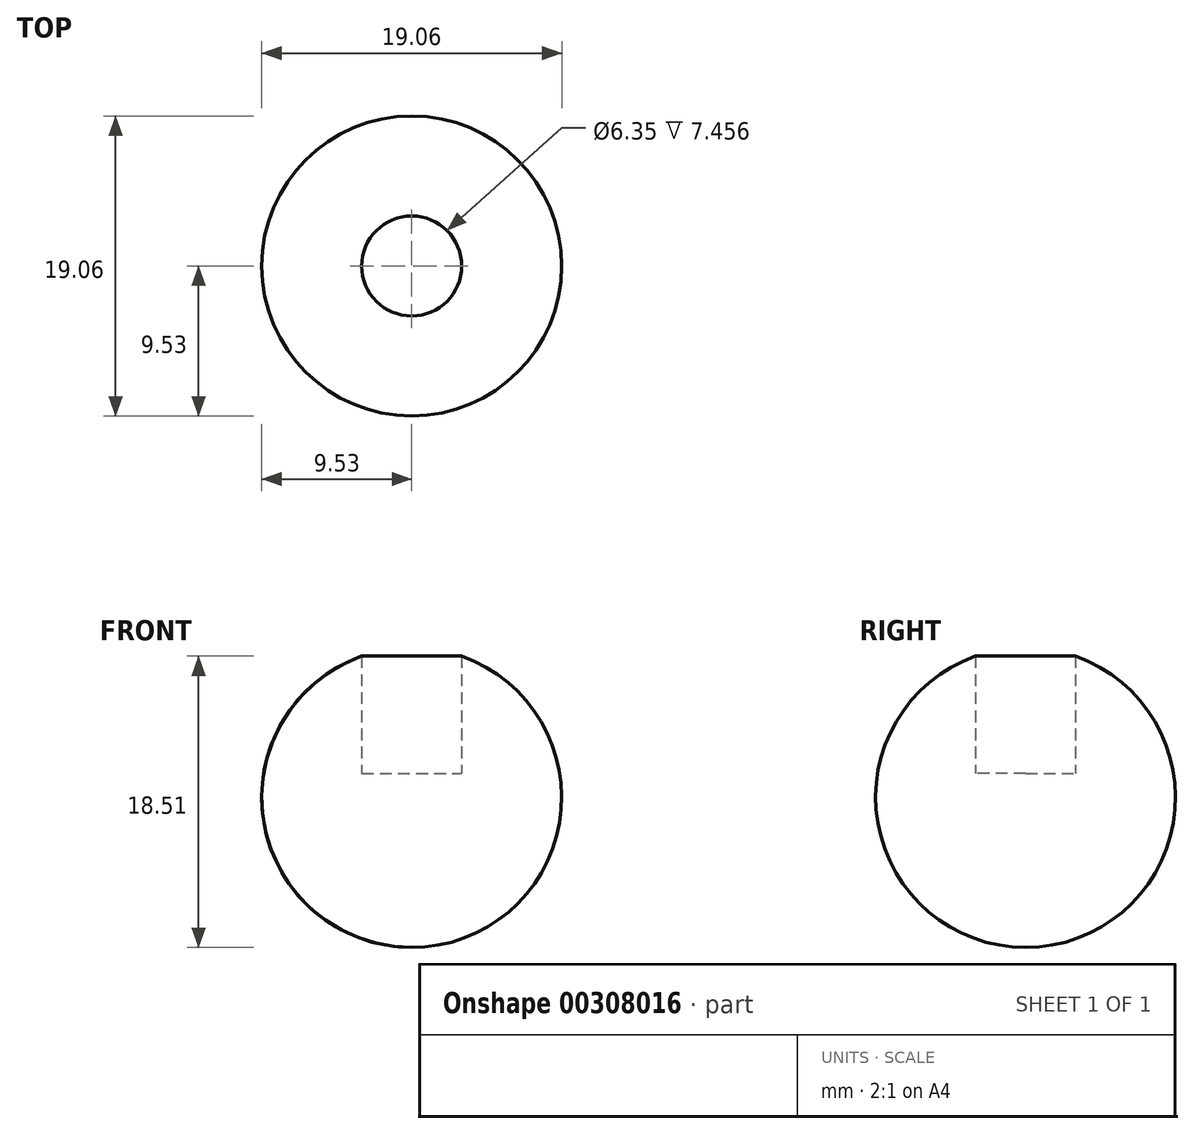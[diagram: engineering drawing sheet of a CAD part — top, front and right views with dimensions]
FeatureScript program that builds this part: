
annotation { "Feature Type Name" : "Feature", "Feature Type Description" : "" }
export const myFeature = defineFeature(function(context is Context, id is Id, definition is map)
    precondition{}
    {
        {
            var Q0;
            Q0=qCreatedBy(makeId("Front.planeOp"),FACE);
            var sketch = newSketch(context, id + "F0", { "sketchPlane" : qUnion([Q0])});
            skArc(sketch, "E0", {"start": v(0, 9.53) * mm, "mid": v(-9.53, 0) * mm, "end": v(0, -9.53) * mm});
            skLineSegment(sketch, "E1", {"start": v(0, 9.53) * mm, "end": v(0, -9.53) * mm});
            skSolve(sketch);
        }
        {
            var Q0;
            Q0=qCreatedBy(makeId("Top.planeOp"),FACE);
            var sketch = newSketch(context, id + "F1", { "sketchPlane" : qUnion([Q0])});
            skCircle(sketch, "E2", {"center": v(0, 0) * mm, "radius": 9.53 * mm});
            skSolve(sketch);
        }
        {
            var Q0;
            Q0=makeQuery(id+"F0.imprint","IMPRINT",FACE,{"disambiguationData":[TD([[makeQuery(id+"F0.imprint","IMPRINT",EDGE,{"derivedFrom":sQuery(id+"F0.wireOp",EDGE,"E0")}),1.0]])]});
            var Q1;
            Q1=sQuery(id+"F1.wireOp",EDGE,"E2");
            revolve(context, id + "F2", {"entities" : qUnion([Q0]), "axis" : qUnion([Q1]), "revolveType" : RevolveType.FULL});
        }
        {
            var Q0;
            Q0=qCreatedBy(makeId("Top.planeOp"),FACE);
            cPlane(context, id + "F3", {"entities" : qUnion([Q0]), "cplaneType" : CPlaneType.OFFSET, "offset" : 1.52 * mm, "width" : 152.4 * mm, "height" : 152.4 * mm});
        }
        {
            var Q0;
            Q0=qCreatedBy(id+"F3.planeOp",FACE);
            var sketch = newSketch(context, id + "F4", { "sketchPlane" : qUnion([Q0])});
            skCircle(sketch, "E3", {"center": v(0, 0) * mm, "radius": 3.18 * mm});
            skSolve(sketch);
        }
        {
            var Q0;
            Q0 = qSketchRegion(id + "F4", true);
            extrude(context, id + "F5", {"entities" : qUnion([Q0]), "operationType" : NewBodyOperationType.REMOVE, "depth" : 10.67 * mm});
        }
        {
            var Q0;
            Q0 = qSketchRegion(id + "F4", true);
            extrude(context, id + "F6", {"entities" : qUnion([Q0]), "operationType" : NewBodyOperationType.REMOVE, "depth" : 6.86 * mm});
        }
    });
